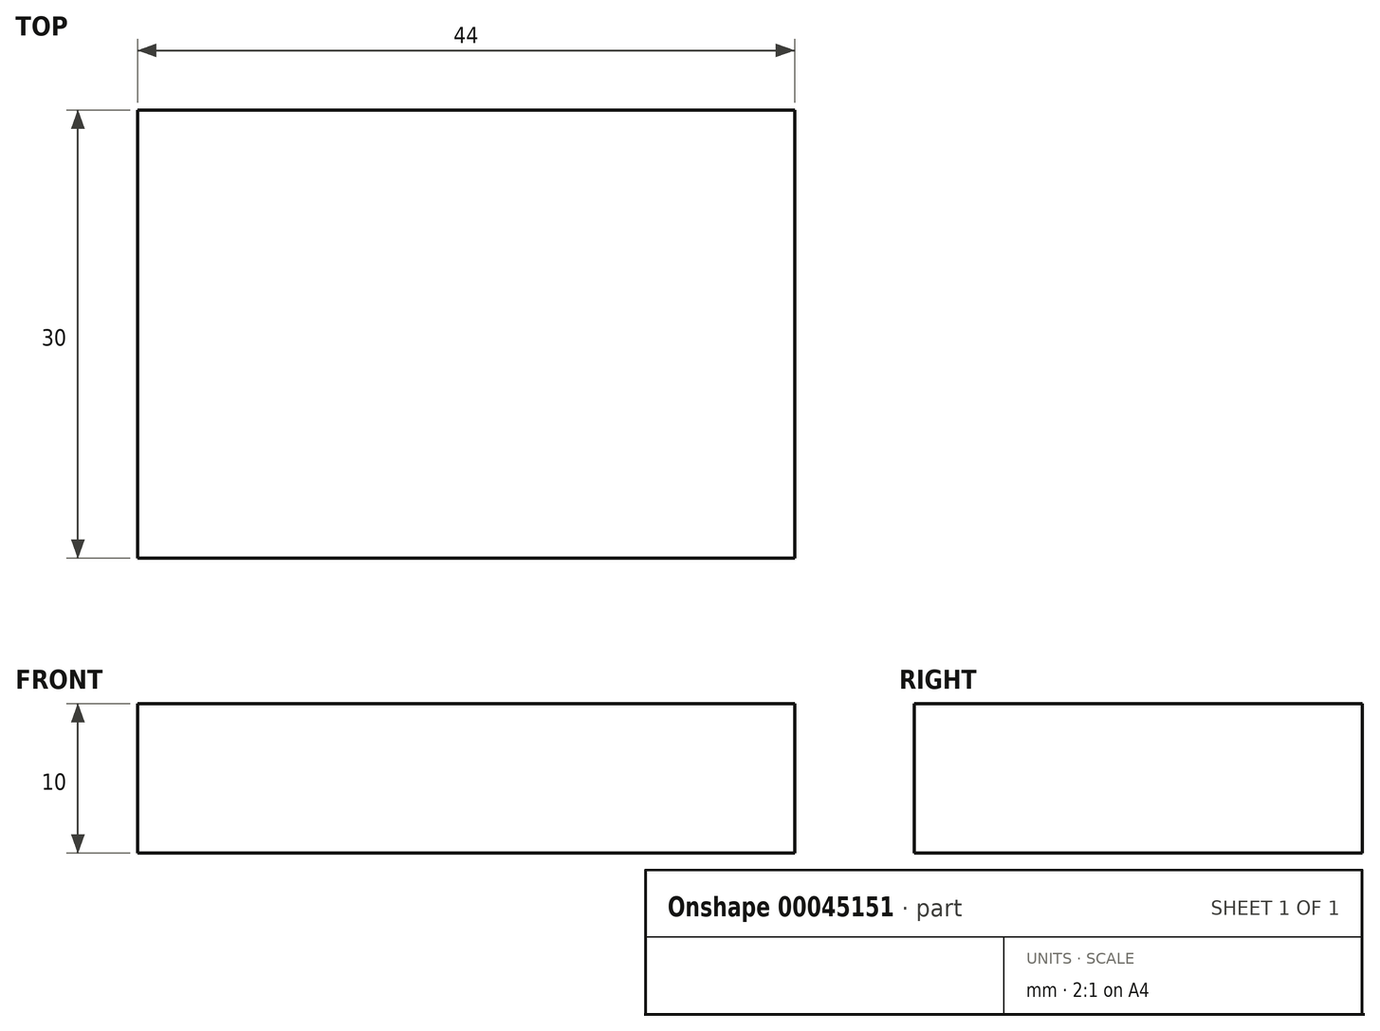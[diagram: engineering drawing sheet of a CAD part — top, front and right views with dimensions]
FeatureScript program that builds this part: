
annotation { "Feature Type Name" : "Feature", "Feature Type Description" : "" }
export const myFeature = defineFeature(function(context is Context, id is Id, definition is map)
    precondition{}
    {
        {
            var Q0;
            Q0=qCreatedBy(makeId("Top.planeOp"),FACE);
            var sketch = newSketch(context, id + "F0", { "sketchPlane" : qUnion([Q0])});
            skLineSegment(sketch, "E0", {"start": v(0, 0) * mm, "end": v(44, 0) * mm});
            skLineSegment(sketch, "E1", {"start": v(0, 0) * mm, "end": v(0, 30) * mm});
            skLineSegment(sketch, "E2", {"start": v(44, 0) * mm, "end": v(44, 30) * mm});
            skLineSegment(sketch, "E3", {"start": v(0, 30) * mm, "end": v(44, 30) * mm});
            skLineSegment(sketch, "E4", {"start": v(22, 30) * mm, "end": v(22, 0) * mm, "construction": true});
            skLineSegment(sketch, "E5", {"start": v(0, 15) * mm, "end": v(44, 15) * mm, "construction": true});
            skLineSegment(sketch, "E6", {"start": v(18.8, 18.84) * mm, "end": v(22, 15) * mm, "construction": true});
            skSolve(sketch);
        }
        {
            var Q0;
            Q0=makeQuery(id+"F0.imprint","IMPRINT",FACE,{"disambiguationData":[TD([[makeQuery(id+"F0.imprint","IMPRINT",EDGE,{"derivedFrom":sQuery(id+"F0.wireOp",EDGE,"E0")}),1.0]])]});
            extrude(context, id + "F1", {"entities" : qUnion([Q0]), "depth" : 10 * mm});
        }
    });
